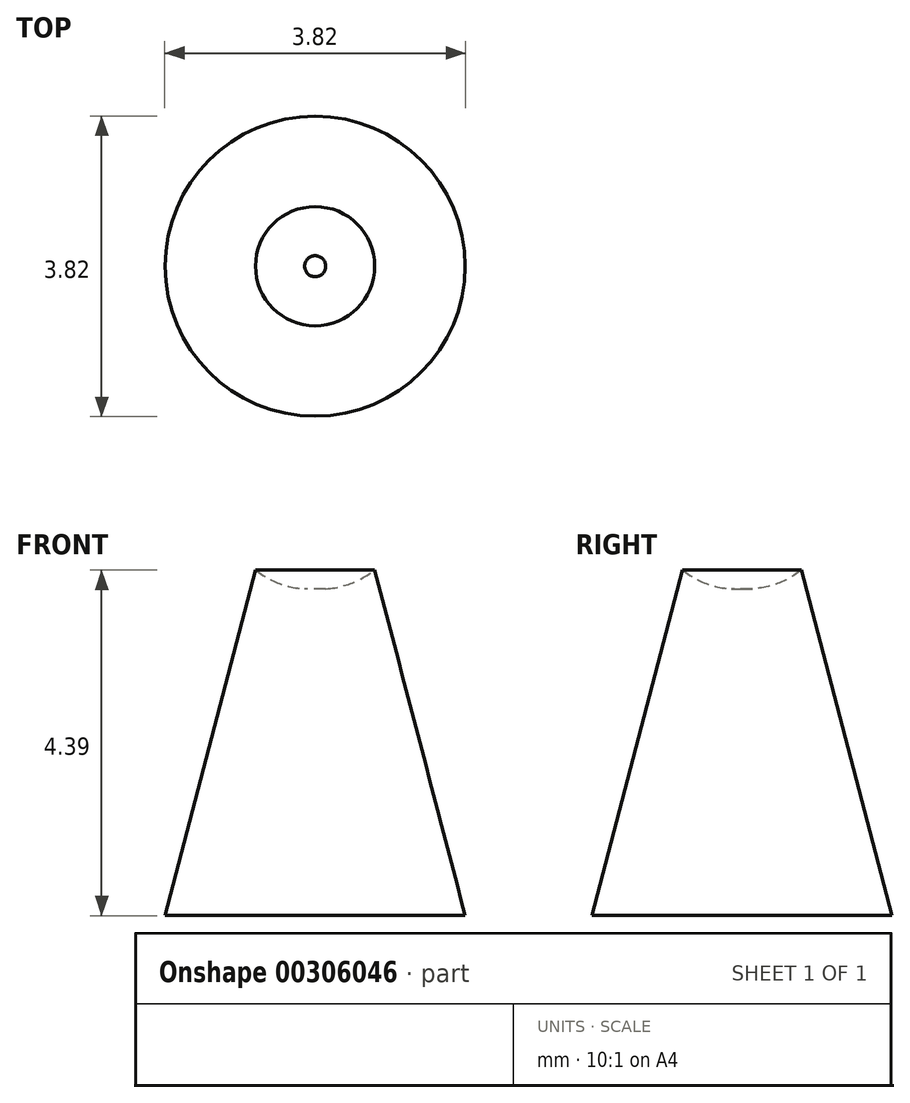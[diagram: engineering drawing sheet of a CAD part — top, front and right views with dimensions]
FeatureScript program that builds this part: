
annotation { "Feature Type Name" : "Feature", "Feature Type Description" : "" }
export const myFeature = defineFeature(function(context is Context, id is Id, definition is map)
    precondition{}
    {
        {
            var Q0;
            Q0=qCreatedBy(makeId("Front.planeOp"),FACE);
            var sketch = newSketch(context, id + "F0", { "sketchPlane" : qUnion([Q0])});
            skLineSegment(sketch, "E0", {"start": v(0, 3.5) * mm, "end": v(0, -2.85) * mm});
            skLineSegment(sketch, "E1", {"start": v(0, -2.85) * mm, "end": v(-1.9, -2.85) * mm});
            skLineSegment(sketch, "E2", {"start": v(-1.9, -2.85) * mm, "end": v(-0.76, 1.54) * mm});
            skArc(sketch, "E3", {"start": v(0, 3.5) * mm, "mid": v(-1.1, 2.8) * mm, "end": v(-0.76, 1.54) * mm});
            skSolve(sketch);
        }
        {
            var Q0;
            Q0=makeQuery(id+"F0.imprint","IMPRINT",FACE,{"disambiguationData":[TD([[makeQuery(id+"F0.imprint","IMPRINT",EDGE,{"derivedFrom":sQuery(id+"F0.wireOp",EDGE,"E0")}),-1.0]])]});
            var Q1;
            Q1=sQuery(id+"F0.wireOp",EDGE,"E0");
            revolve(context, id + "F1", {"entities" : qUnion([Q0]), "axis" : qUnion([Q1]), "revolveType" : RevolveType.FULL});
        }
    });
